# Revit family: 873-00-001-DN700-800
name_source: partatom
category: Pipe Accessories
units: mm (PartAtom-declared; Revit-internal decimal feet)

## family parameters
Always vertical = Yes
Cut with Voids When Loaded = No
Part Type = Valve - Breaks Into
Round Connector Dimension = Use Diameter
Shared = No
Work Plane-Based = No

## types (4) — shared parameters
873-0700-00-041000 = DN700_PN10
873-0700-00-141000 = DN700_PN16
873-0800-00-041000 = DN800_PN10
873-0800-00-141000 = DN800_PN16
Angle = 22.50°
Body_Wallthicknss = 10 mm  [stored 0.0328084 ft]
Description_ = AVK DISMANTLING JOINT
Flange_thickness = 20 mm  [stored 0.0656168 ft]
Search_table = 873-00-001-DN700-800
URL product pages = https://www.avkvalves.com

## per-type parameters (varying)
| type | A | DN | Id(Radius) | L | T | d1 | d2 |
| DN700_PN10 | 300 mm  [stored 0.984252 ft] | 700 mm  [stored 2.29659 ft] | 350 mm  [stored 1.14829 ft] | 480 mm  [stored 1.5748 ft] | 27 mm  [stored 0.0885827 ft] | 840 mm  [stored 2.75591 ft] | 448 mm |
| DN700_PN16 | 300 mm  [stored 0.984252 ft] | 700 mm  [stored 2.29659 ft] | 350 mm  [stored 1.14829 ft] | 500 mm  [stored 1.64042 ft] | 33 mm  [stored 0.108268 ft] | 840 mm  [stored 2.75591 ft] | 455 mm |
| DN800_PN10 | 315 mm  [stored 1.03346 ft] | 800 mm  [stored 2.62467 ft] | 400 mm  [stored 1.31234 ft] | 500 mm  [stored 1.64042 ft] | 30 mm  [stored 0.0984252 ft] | 950 mm  [stored 3.1168 ft] | 505 mm  [stored 1.65682 ft] |
| DN800_PN16 | 315 mm  [stored 1.03346 ft] | 800 mm  [stored 2.62467 ft] | 400 mm  [stored 1.31234 ft] | 530 mm  [stored 1.73885 ft] | 36 mm  [stored 0.11811 ft] | 950 mm  [stored 3.1168 ft] | 513 mm |

note: [stored X ft] marks values corroborated as IEEE doubles in the binary element streams (Revit-internal decimal feet)

## geometry (parser evidence)
native form markers: Sweep x14
no freeform markers — native parametric forms only
